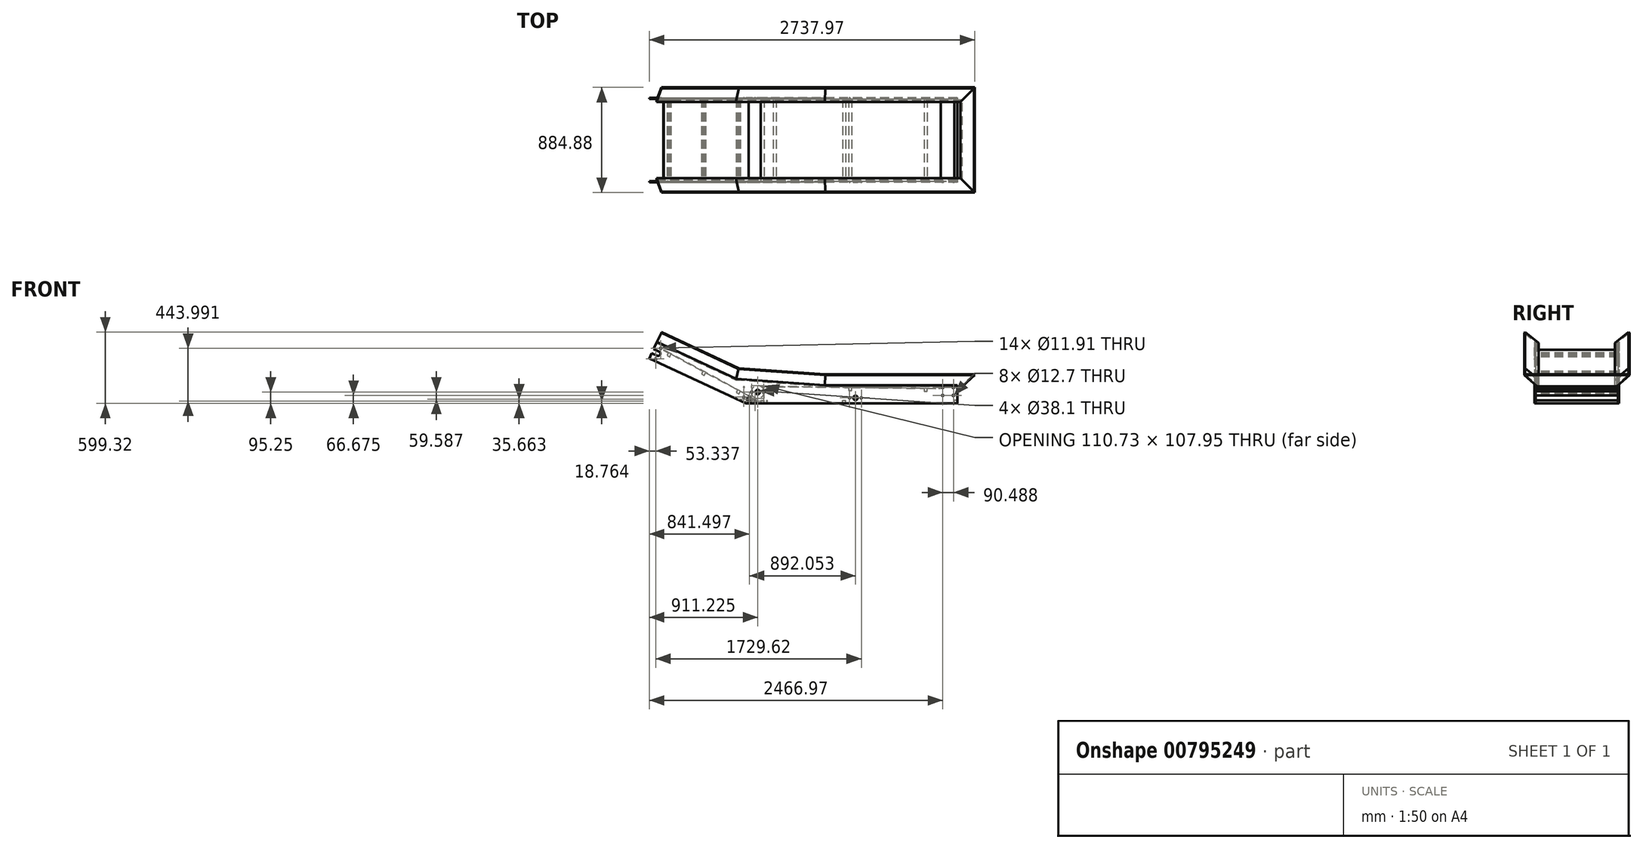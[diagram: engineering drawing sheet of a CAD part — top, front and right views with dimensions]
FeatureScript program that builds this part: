
annotation { "Feature Type Name" : "Feature", "Feature Type Description" : "" }
export const myFeature = defineFeature(function(context is Context, id is Id, definition is map)
    precondition{}
    {
        {
            var Q0;
            Q0=qCreatedBy(makeId("Front.planeOp"),FACE);
            var sketch = newSketch(context, id + "F0", { "sketchPlane" : qUnion([Q0])});
            skLineSegment(sketch, "E0.bottom", {"start": v(0, 0) * mm, "end": v(-1778, 0) * mm});
            skLineSegment(sketch, "E0.top", {"start": v(0, 152.4) * mm, "end": v(-1115.54, 152.4) * mm});
            skLineSegment(sketch, "E0.left", {"start": v(0, 0) * mm, "end": v(0, 152.4) * mm});
            skLineSegment(sketch, "E1.bottom", {"start": v(-2526.4, 517.14) * mm, "end": v(-1862.08, 207.36) * mm});
            skLineSegment(sketch, "E1.top", {"start": v(-2590.8, 379.01) * mm, "end": v(-1778, 0) * mm});
            skLineSegment(sketch, "E1.left", {"start": v(-2526.4, 517.14) * mm, "end": v(-2590.8, 379.01) * mm});
            skArc(sketch, "E2", {"start": v(-2524.63, 400.7) * mm, "mid": v(-2499.32, 409.92) * mm, "end": v(-2508.53, 435.24) * mm});
            skLineSegment(sketch, "E3", {"start": v(-2495.7, 462.76) * mm, "end": v(-2537.46, 373.2) * mm, "construction": true});
            skCircle(sketch, "E4", {"center": v(-2495.7, 462.76) * mm, "radius": 5.95 * mm});
            skCircle(sketch, "E5", {"center": v(-2537.46, 373.2) * mm, "radius": 5.95 * mm});
            skCircle(sketch, "E6", {"center": v(-123.83, 133.35) * mm, "radius": 6.35 * mm});
            skCircle(sketch, "E7.0.1.0", {"center": v(-123.83, 66.68) * mm, "radius": 6.35 * mm});
            skCircle(sketch, "E7.1.0.0", {"center": v(-33.34, 133.35) * mm, "radius": 6.35 * mm});
            skCircle(sketch, "E7.1.1.0", {"center": v(-33.34, 66.68) * mm, "radius": 6.35 * mm});
            skArc(sketch, "E8", {"start": v(-2489.95, 461.23) * mm, "mid": v(-2562.62, 439.44) * mm, "end": v(-2532.6, 369.76) * mm, "construction": true});
            skArc(sketch, "E9", {"start": v(-1678.96, 146.05) * mm, "mid": v(-1730.37, 95.1) * mm, "end": v(-1678.68, 44.46) * mm, "construction": true});
            skArc(sketch, "E10", {"start": v(-1759.95, 12.6) * mm, "mid": v(-1726.57, 24.34) * mm, "end": v(-1737.3, 58.05) * mm, "construction": true});
            skArc(sketch, "E11", {"start": v(35.37, 74.62) * mm, "mid": v(60.32, 100.08) * mm, "end": v(35.23, 125.41) * mm, "construction": true});
            skLineSegment(sketch, "E12", {"start": v(-2492.59, 462.75) * mm, "end": v(-1737.3, 58.05) * mm, "construction": true});
            skLineSegment(sketch, "E13", {"start": v(-1759.95, 12.6) * mm, "end": v(-2537.88, 371.85) * mm, "construction": true});
            skLineSegment(sketch, "E14", {"start": v(-1678.96, 146.05) * mm, "end": v(35.23, 125.41) * mm, "construction": true});
            skLineSegment(sketch, "E15", {"start": v(35.37, 74.62) * mm, "end": v(-1678.68, 44.46) * mm, "construction": true});
            skCircle(sketch, "E16", {"center": v(-1679.58, 95.25) * mm, "radius": 19.05 * mm});
            skCircle(sketch, "E17", {"center": v(-1749.3, 35.66) * mm, "radius": 19.05 * mm});
            skLineSegment(sketch, "E18", {"start": v(-1728.99, 95.25) * mm, "end": v(-1630.16, 95.25) * mm, "construction": true});
            skCircle(sketch, "E19", {"center": v(-1728.99, 95.25) * mm, "radius": 5.95 * mm});
            skCircle(sketch, "E20", {"center": v(-1630.16, 95.25) * mm, "radius": 5.95 * mm});
            skLineSegment(sketch, "E21", {"start": v(-1795.73, 52.56) * mm, "end": v(-1702.87, 18.76) * mm, "construction": true});
            skCircle(sketch, "E22", {"center": v(-1795.73, 52.56) * mm, "radius": 5.95 * mm});
            skCircle(sketch, "E23", {"center": v(-1702.87, 18.76) * mm, "radius": 5.95 * mm});
            skLineSegment(sketch, "E24", {"start": v(-1744.21, 152.4) * mm, "end": v(-1862.08, 207.36) * mm, "construction": true});
            skLineSegment(sketch, "E25", {"start": v(-1744.21, 152.4) * mm, "end": v(-1115.54, 152.4) * mm, "construction": true});
            skLineSegment(sketch, "E26", {"start": v(-1862.08, 207.36) * mm, "end": v(-1115.54, 152.4) * mm});
            skCircle(sketch, "E27", {"center": v(-857.25, 46.2) * mm, "radius": 12.7 * mm, "construction": true});
            skCircle(sketch, "E28", {"center": v(-857.25, 46.2) * mm, "radius": 19.05 * mm});
            skLineSegment(sketch, "E29", {"start": v(-906.66, 46.2) * mm, "end": v(-807.84, 46.2) * mm, "construction": true});
            skCircle(sketch, "E30", {"center": v(-906.66, 46.2) * mm, "radius": 5.95 * mm});
            skCircle(sketch, "E31", {"center": v(-807.84, 46.2) * mm, "radius": 5.95 * mm});
            skLineSegment(sketch, "E32", {"start": v(-2508.53, 435.24) * mm, "end": v(-2554.57, 456.7) * mm});
            skLineSegment(sketch, "E33", {"start": v(-2570.67, 422.18) * mm, "end": v(-2524.63, 400.7) * mm});
            skSolve(sketch);
        }
        {
            var Q0;
            Q0=makeQuery(id+"F0.imprint","IMPRINT",FACE,{"disambiguationData":[TD([[makeQuery(id+"F0.imprint","IMPRINT",EDGE,{"derivedFrom":sQuery(id+"F0.wireOp",EDGE,"E0.top")}),1.0]])]});
            extrude(context, id + "F1", {"entities" : qUnion([Q0]), "oppositeDirection" : true, "depth" : 711.2 * mm, "offsetDistance" : 25.4 * mm});
        }
        {
            var Q0;
            Q0=makeQuery(id+"F1.opExtrude","SWEPT_FACE",FACE,{"disambiguationData":[OSD([sQuery(id+"F0.wireOp",EDGE,"E0.left")])]});
            var sketch = newSketch(context, id + "F2", { "sketchPlane" : qUnion([Q0])});
            skLineSegment(sketch, "E34.bottom", {"start": v(9.53, 0) * mm, "end": v(701.68, 0) * mm});
            skLineSegment(sketch, "E34.top", {"start": v(9.53, 692.15) * mm, "end": v(701.68, 692.15) * mm});
            skLineSegment(sketch, "E34.left", {"start": v(9.53, 0) * mm, "end": v(9.53, 692.15) * mm});
            skLineSegment(sketch, "E34.right", {"start": v(701.68, 0) * mm, "end": v(701.68, 692.15) * mm});
            skSolve(sketch);
        }
        {
            var Q0;
            Q0 = qSketchRegion(id + "F2", true);
            extrude(context, id + "F3", {"entities" : qUnion([Q0]), "operationType" : NewBodyOperationType.REMOVE, "oppositeDirection" : true, "depth" : 2667 * mm, "offsetDistance" : 25.4 * mm});
        }
        {
            var Q0;
            {var subQ5=sQuery(id+"F0.wireOp",EDGE,"E0.left");Q0=makeQuery(id+"F0.imprint","IMPRINT",FACE,{"disambiguationData":[TD([[makeQuery(id+"F0.imprint","IMPRINT",EDGE,{"derivedFrom":subQ5}),1.0]])]});}
            cPlane(context, id + "F4", {"entities" : qUnion([Q0]), "cplaneType" : CPlaneType.OFFSET, "offset" : 9.52 * mm, "oppositeDirection" : true, "width" : 152.4 * mm, "height" : 152.4 * mm});
        }
        {
            var Q0;
            Q0=qCreatedBy(id+"F4.planeOp",FACE);
            var sketch = newSketch(context, id + "F5", { "sketchPlane" : qUnion([Q0])});
            skArc(sketch, "E35", {"start": v(-2492.59, 462.75) * mm, "mid": v(-2563.25, 438.05) * mm, "end": v(-2532.6, 369.76) * mm, "construction": true});
            skArc(sketch, "E36", {"start": v(-1678.96, 146.05) * mm, "mid": v(-1730.37, 95.1) * mm, "end": v(-1678.68, 44.46) * mm, "construction": true});
            skArc(sketch, "E37", {"start": v(-1759.95, 12.6) * mm, "mid": v(-1726.57, 24.34) * mm, "end": v(-1737.3, 58.05) * mm, "construction": true});
            skArc(sketch, "E38", {"start": v(35.37, 74.62) * mm, "mid": v(60.32, 100.08) * mm, "end": v(35.23, 125.41) * mm, "construction": true});
            skLineSegment(sketch, "E39", {"start": v(-2492.59, 462.75) * mm, "end": v(-2489.92, 461.32) * mm});
            skLineSegment(sketch, "E40", {"start": v(-1759.95, 12.6) * mm, "end": v(-2537.88, 371.85) * mm, "construction": true});
            skLineSegment(sketch, "E41", {"start": v(-1678.96, 146.05) * mm, "end": v(-139.8, 127.52) * mm});
            skLineSegment(sketch, "E42", {"start": v(35.37, 74.62) * mm, "end": v(-1678.68, 44.46) * mm, "construction": true});
            skLineSegment(sketch, "E43.0", {"start": v(-1654.43, 142.7) * mm, "end": v(-139.84, 124.47) * mm});
            skLineSegment(sketch, "E44", {"start": v(-914.7, 133.8) * mm, "end": v(-915, 108.4) * mm});
            skLineSegment(sketch, "E45", {"start": v(-915, 108.4) * mm, "end": v(-889.6, 108.1) * mm});
            skLineSegment(sketch, "E46", {"start": v(-889.6, 108.1) * mm, "end": v(-889.3, 133.5) * mm});
            skLineSegment(sketch, "E47", {"start": v(-889.3, 133.5) * mm, "end": v(-914.7, 133.8) * mm});
            skLineSegment(sketch, "E48", {"start": v(-1549.64, 141.44) * mm, "end": v(-1549.95, 116.04) * mm});
            skLineSegment(sketch, "E49", {"start": v(-1549.95, 116.04) * mm, "end": v(-1524.55, 115.74) * mm});
            skLineSegment(sketch, "E50", {"start": v(-1524.55, 115.74) * mm, "end": v(-1524.25, 141.14) * mm});
            skLineSegment(sketch, "E51", {"start": v(-1524.25, 141.14) * mm, "end": v(-1549.64, 141.44) * mm});
            skLineSegment(sketch, "E52", {"start": v(-279.74, 126.15) * mm, "end": v(-280.04, 100.76) * mm});
            skLineSegment(sketch, "E53", {"start": v(-280.04, 100.76) * mm, "end": v(-254.64, 100.45) * mm});
            skLineSegment(sketch, "E54", {"start": v(-254.64, 100.45) * mm, "end": v(-254.34, 125.85) * mm});
            skLineSegment(sketch, "E55", {"start": v(-254.34, 125.85) * mm, "end": v(-279.74, 126.15) * mm});
            skLineSegment(sketch, "E56", {"start": v(-2430.99, 426.29) * mm, "end": v(-2442.99, 403.9) * mm});
            skLineSegment(sketch, "E57", {"start": v(-2442.99, 403.9) * mm, "end": v(-2420.6, 391.9) * mm});
            skLineSegment(sketch, "E58", {"start": v(-2420.6, 391.9) * mm, "end": v(-2408.6, 414.3) * mm});
            skLineSegment(sketch, "E59", {"start": v(-2408.6, 414.3) * mm, "end": v(-2430.99, 426.29) * mm});
            skLineSegment(sketch, "E60", {"start": v(-2139.94, 270.33) * mm, "end": v(-2151.93, 247.95) * mm});
            skLineSegment(sketch, "E61", {"start": v(-2151.93, 247.95) * mm, "end": v(-2129.55, 235.95) * mm});
            skLineSegment(sketch, "E62", {"start": v(-2129.55, 235.95) * mm, "end": v(-2117.55, 258.34) * mm});
            skLineSegment(sketch, "E63", {"start": v(-2117.55, 258.34) * mm, "end": v(-2139.94, 270.33) * mm});
            skLineSegment(sketch, "E64", {"start": v(-1848.89, 114.38) * mm, "end": v(-1860.88, 92) * mm});
            skLineSegment(sketch, "E65", {"start": v(-1860.88, 92) * mm, "end": v(-1838.5, 80) * mm});
            skLineSegment(sketch, "E66", {"start": v(-1838.5, 80) * mm, "end": v(-1826.5, 102.39) * mm});
            skLineSegment(sketch, "E67", {"start": v(-1826.5, 102.39) * mm, "end": v(-1848.89, 114.38) * mm});
            skLineSegment(sketch, "E68", {"start": v(-2472.18, 448.36) * mm, "end": v(-2470.74, 451.05) * mm});
            skLineSegment(sketch, "E69", {"start": v(-1756.84, 65.06) * mm, "end": v(-1755.4, 67.75) * mm});
            skLineSegment(sketch, "E70", {"start": v(-1654.43, 142.7) * mm, "end": v(-1654.4, 145.75) * mm});
            skLineSegment(sketch, "E71", {"start": v(-139.84, 124.47) * mm, "end": v(-139.8, 127.52) * mm});
            skLineSegment(sketch, "E72.trimOffspring", {"start": v(-2472.18, 448.36) * mm, "end": v(-1756.84, 65.06) * mm});
            skLineSegment(sketch, "E73.trimOffspring", {"start": v(-2470.74, 451.05) * mm, "end": v(-1755.4, 67.75) * mm});
            skLineSegment(sketch, "E74.bottom", {"start": v(0, 0) * mm, "end": v(-25.4, 0) * mm});
            skLineSegment(sketch, "E74.top", {"start": v(0, 25.4) * mm, "end": v(-25.4, 25.4) * mm});
            skLineSegment(sketch, "E74.left", {"start": v(0, 0) * mm, "end": v(0, 25.4) * mm});
            skLineSegment(sketch, "E74.right", {"start": v(-25.4, 0) * mm, "end": v(-25.4, 25.4) * mm});
            skLineSegment(sketch, "E75.bottom", {"start": v(-1651, 0) * mm, "end": v(-1625.6, 0) * mm});
            skLineSegment(sketch, "E75.top", {"start": v(-1651, 25.4) * mm, "end": v(-1625.6, 25.4) * mm});
            skLineSegment(sketch, "E75.left", {"start": v(-1651, 0) * mm, "end": v(-1651, 25.4) * mm});
            skLineSegment(sketch, "E75.right", {"start": v(-1625.6, 0) * mm, "end": v(-1625.6, 25.4) * mm});
            skPoint(sketch, "E76.oppositeSnap0", {"position": v(-1638.3, 25.4) * mm});
            skLineSegment(sketch, "E76.bottom", {"start": v(-965.2, 0) * mm, "end": v(-939.8, 0) * mm});
            skLineSegment(sketch, "E76.top", {"start": v(-965.2, 25.4) * mm, "end": v(-939.8, 25.4) * mm});
            skLineSegment(sketch, "E76.left", {"start": v(-965.2, 0) * mm, "end": v(-965.2, 25.4) * mm});
            skLineSegment(sketch, "E76.right", {"start": v(-939.8, 0) * mm, "end": v(-939.8, 25.4) * mm});
            skSolve(sketch);
        }
        {
            var Q0;
            Q0 = qSketchRegion(id + "F5", true);
            extrude(context, id + "F6", {"entities" : qUnion([Q0]), "oppositeDirection" : true, "depth" : 692.15 * mm, "offsetDistance" : 25.4 * mm});
        }
        {
            var Q0;
            {var subQ0=sQuery(id+"F0.wireOp",EDGE,"E1.left");Q0=makeQuery(id+"F3.boolean.opBoolean","SPLIT",FACE,{"disambiguationData":[TD([makeQuery(id+"F3.opExtrude","SWEPT_FACE",FACE,{"disambiguationData":[OSD([sQuery(id+"F2.wireOp",EDGE,"E34.left")])]})])],"derivedFrom":makeQuery(id+"F1.opExtrude","SWEPT_FACE",FACE,{"disambiguationData":[OSD([subQ0])]})});}
            var sketch = newSketch(context, id + "F7", { "sketchPlane" : qUnion([Q0])});
            skLineSegment(sketch, "E77.bottom", {"start": v(79.9, -508.33) * mm, "end": v(86.84, -514.91) * mm});
            skLineSegment(sketch, "E77.left", {"start": v(86.84, -514.91) * mm, "end": v(-9.52, -599.02) * mm});
            skLineSegment(sketch, "E77.right", {"start": v(79.9, -508.33) * mm, "end": v(-34.92, -608.54) * mm});
            skLineSegment(sketch, "E78", {"start": v(-9.52, -599.02) * mm, "end": v(-20.44, -608.54) * mm});
            skLineSegment(sketch, "E79", {"start": v(-34.93, -608.54) * mm, "end": v(-20.44, -608.54) * mm});
            skSolve(sketch);
        }
        {
            var Q0;
            {var subQ2=sQuery(id+"F0.wireOp",EDGE,"E0.top");Q0=makeQuery(id+"F3.boolean.opBoolean","SPLIT",FACE,{"disambiguationData":[TD([makeQuery(id+"F3.opExtrude","SWEPT_FACE",FACE,{"disambiguationData":[OSD([sQuery(id+"F2.wireOp",EDGE,"E34.left")])]})])],"derivedFrom":makeQuery(id+"F1.opExtrude","SWEPT_FACE",FACE,{"disambiguationData":[OSD([subQ2])]})});}
            var sketch = newSketch(context, id + "F8", { "sketchPlane" : qUnion([Q0])});
            skLineSegment(sketch, "E80", {"start": v(0, 9.53) * mm, "end": v(50.8, 9.53) * mm});
            skLineSegment(sketch, "E81", {"start": v(50.8, 9.53) * mm, "end": v(50.8, 701.68) * mm});
            skLineSegment(sketch, "E82", {"start": v(50.8, 701.68) * mm, "end": v(0, 701.68) * mm});
            skSolve(sketch);
        }
        {
            var Q0;
            {var subQ1=sQuery(id+"F7.wireOp",EDGE,"E77.bottom");Q0=makeQuery(id+"F7.imprint","IMPRINT",FACE,{"disambiguationData":[TD([[makeQuery(id+"F7.imprint","IMPRINT",EDGE,{"derivedFrom":subQ1}),-1.0]])]});}
            var Q1;
            Q1=makeQuery(id+"F3.boolean.opBoolean","INTERSECT",EDGE,{"derivedFrom":[makeQuery(id+"F1.opExtrude","SWEPT_FACE",FACE,{"disambiguationData":[OSD([sQuery(id+"F0.wireOp",EDGE,"E1.bottom")])]}),makeQuery(id+"F3.opExtrude","SWEPT_FACE",FACE,{"disambiguationData":[OSD([sQuery(id+"F2.wireOp",EDGE,"E34.left")])]})]});
            var Q2;
            Q2=makeQuery(id+"F3.boolean.opBoolean","INTERSECT",EDGE,{"derivedFrom":[makeQuery(id+"F1.opExtrude","SWEPT_FACE",FACE,{"disambiguationData":[OSD([sQuery(id+"F0.wireOp",EDGE,"E26")])]}),makeQuery(id+"F3.opExtrude","SWEPT_FACE",FACE,{"disambiguationData":[OSD([sQuery(id+"F2.wireOp",EDGE,"E34.left")])]})]});
            var Q3;
            Q3=makeQuery(id+"F3.boolean.opBoolean","INTERSECT",EDGE,{"derivedFrom":[makeQuery(id+"F1.opExtrude","SWEPT_FACE",FACE,{"disambiguationData":[OSD([sQuery(id+"F0.wireOp",EDGE,"E0.top")])]}),makeQuery(id+"F3.opExtrude","SWEPT_FACE",FACE,{"disambiguationData":[OSD([sQuery(id+"F2.wireOp",EDGE,"E34.left")])]})]});
            var Q4;
            Q4=sQuery(id+"F8.wireOp",EDGE,"E80");
            var Q5;
            Q5=sQuery(id+"F8.wireOp",EDGE,"E81");
            var Q6;
            Q6=sQuery(id+"F8.wireOp",EDGE,"E82");
            var Q7;
            Q7=makeQuery(id+"F3.boolean.opBoolean","INTERSECT",EDGE,{"derivedFrom":[makeQuery(id+"F1.opExtrude","SWEPT_FACE",FACE,{"disambiguationData":[OSD([sQuery(id+"F0.wireOp",EDGE,"E0.top")])]}),makeQuery(id+"F3.opExtrude","SWEPT_FACE",FACE,{"disambiguationData":[OSD([sQuery(id+"F2.wireOp",EDGE,"E34.right")])]})]});
            var Q8;
            Q8=makeQuery(id+"F3.boolean.opBoolean","INTERSECT",EDGE,{"derivedFrom":[makeQuery(id+"F1.opExtrude","SWEPT_FACE",FACE,{"disambiguationData":[OSD([sQuery(id+"F0.wireOp",EDGE,"E26")])]}),makeQuery(id+"F3.opExtrude","SWEPT_FACE",FACE,{"disambiguationData":[OSD([sQuery(id+"F2.wireOp",EDGE,"E34.right")])]})]});
            var Q9;
            Q9=makeQuery(id+"F3.boolean.opBoolean","INTERSECT",EDGE,{"derivedFrom":[makeQuery(id+"F1.opExtrude","SWEPT_FACE",FACE,{"disambiguationData":[OSD([sQuery(id+"F0.wireOp",EDGE,"E1.bottom")])]}),makeQuery(id+"F3.opExtrude","SWEPT_FACE",FACE,{"disambiguationData":[OSD([sQuery(id+"F2.wireOp",EDGE,"E34.right")])]})]});
            sweep(context, id + "F9", {"profiles" : qUnion([Q0]), "path" : qUnion([Q1, Q2, Q3, Q4, Q5, Q6, Q7, Q8, Q9])});
        }
        {
            var Q0;
            Q0=makeQuery(id+"F1.opExtrude","CAP_FACE",FACE,{"disambiguationData":[OSD([sQuery(id+"F0.wireOp",EDGE,"E0.bottom"),sQuery(id+"F0.wireOp",EDGE,"E0.top"),sQuery(id+"F0.wireOp",EDGE,"E0.left"),sQuery(id+"F0.wireOp",EDGE,"E1.bottom"),sQuery(id+"F0.wireOp",EDGE,"E1.top"),sQuery(id+"F0.wireOp",EDGE,"E1.left"),sQuery(id+"F0.wireOp",EDGE,"E2"),sQuery(id+"F0.wireOp",EDGE,"E4"),sQuery(id+"F0.wireOp",EDGE,"E5"),sQuery(id+"F0.wireOp",EDGE,"E6"),sQuery(id+"F0.wireOp",EDGE,"E7.0.1.0"),sQuery(id+"F0.wireOp",EDGE,"E7.1.0.0"),sQuery(id+"F0.wireOp",EDGE,"E7.1.1.0"),sQuery(id+"F0.wireOp",EDGE,"E16"),sQuery(id+"F0.wireOp",EDGE,"E17"),sQuery(id+"F0.wireOp",EDGE,"E19"),sQuery(id+"F0.wireOp",EDGE,"E20"),sQuery(id+"F0.wireOp",EDGE,"E22"),sQuery(id+"F0.wireOp",EDGE,"E23"),sQuery(id+"F0.wireOp",EDGE,"E26"),sQuery(id+"F0.wireOp",EDGE,"E28"),sQuery(id+"F0.wireOp",EDGE,"E30"),sQuery(id+"F0.wireOp",EDGE,"E31")])],"isStart":false});
            var sketch = newSketch(context, id + "F10", { "sketchPlane" : qUnion([Q0])});
            skCircle(sketch, "E83.MirrorC", {"center": v(1602.45, 18.76) * mm, "radius": 4.76 * mm});
            skCircle(sketch, "E84.MirrorC", {"center": v(1602.45, 135.72) * mm, "radius": 4.76 * mm});
            skCircle(sketch, "E85.MirrorC", {"center": v(1795.73, 135.72) * mm, "radius": 4.76 * mm});
            skArc(sketch, "E86", {"start": v(1625.75, 91.26) * mm, "mid": v(1679.58, 41.28) * mm, "end": v(1733.4, 91.26) * mm});
            skArc(sketch, "E87", {"start": v(1625.75, 99.24) * mm, "mid": v(1624.21, 95.25) * mm, "end": v(1625.75, 91.26) * mm});
            skArc(sketch, "E88", {"start": v(1733.4, 91.26) * mm, "mid": v(1734.94, 95.25) * mm, "end": v(1733.4, 99.24) * mm});
            skArc(sketch, "E89.trimOffspring", {"start": v(1733.4, 99.24) * mm, "mid": v(1679.58, 149.23) * mm, "end": v(1625.75, 99.24) * mm});
            skLineSegment(sketch, "E90", {"start": v(1730.25, 35.66) * mm, "end": v(1730.25, 0) * mm});
            skLineSegment(sketch, "E91", {"start": v(1730.25, 0) * mm, "end": v(1768.35, 0) * mm});
            skLineSegment(sketch, "E92", {"start": v(1768.35, 0) * mm, "end": v(1768.35, 35.66) * mm});
            skArc(sketch, "E93", {"start": v(1730.25, 35.66) * mm, "mid": v(1749.3, 54.71) * mm, "end": v(1768.35, 35.66) * mm});
            skCircle(sketch, "E94", {"center": v(1702.87, 18.76) * mm, "radius": 5.95 * mm});
            skCircle(sketch, "E95", {"center": v(1795.73, 52.56) * mm, "radius": 5.95 * mm});
            skSolve(sketch);
        }
        {
            var Q0;
            Q0 = qSketchRegion(id + "F10", true);
            extrude(context, id + "F11", {"entities" : qUnion([Q0]), "operationType" : NewBodyOperationType.REMOVE, "oppositeDirection" : true, "depth" : 9.52 * mm, "offsetDistance" : 25.4 * mm});
        }
    });
